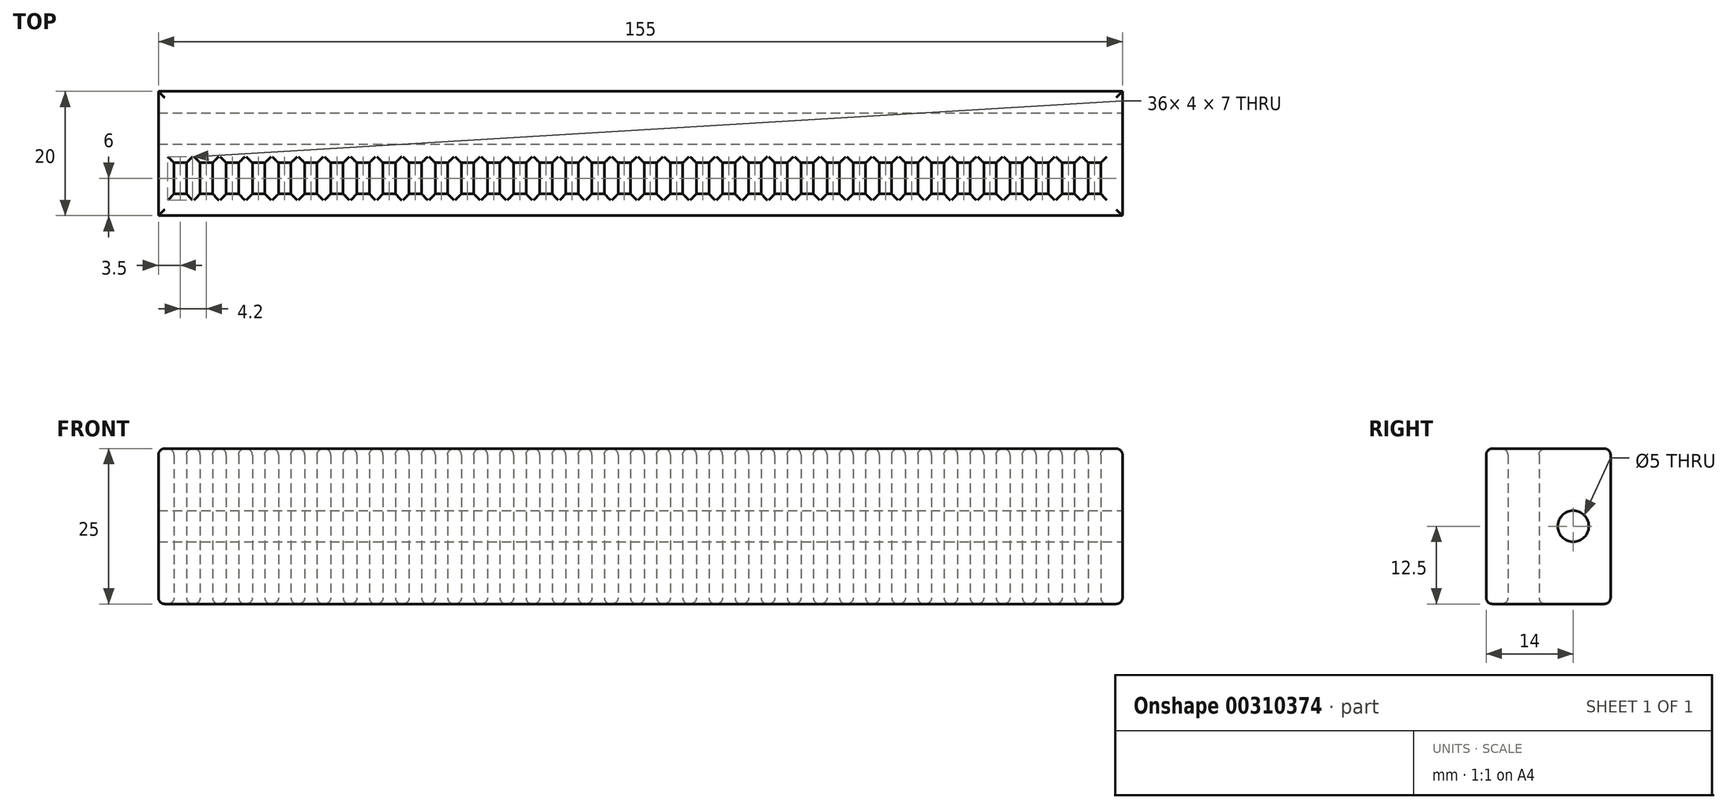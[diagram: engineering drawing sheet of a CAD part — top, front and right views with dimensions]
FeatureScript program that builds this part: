
annotation { "Feature Type Name" : "Feature", "Feature Type Description" : "" }
export const myFeature = defineFeature(function(context is Context, id is Id, definition is map)
    precondition{}
    {
        {
            var Q0;
            Q0=qCreatedBy(makeId("Top.planeOp"),FACE);
            var sketch = newSketch(context, id + "F0", { "sketchPlane" : qUnion([Q0])});
            skLineSegment(sketch, "E0.bottom", {"start": v(77.5, -10) * mm, "end": v(-77.5, -10) * mm});
            skLineSegment(sketch, "E0.top", {"start": v(77.5, 10) * mm, "end": v(-77.5, 10) * mm});
            skLineSegment(sketch, "E0.left", {"start": v(77.5, -10) * mm, "end": v(77.5, 10) * mm});
            skLineSegment(sketch, "E0.right", {"start": v(-77.5, -10) * mm, "end": v(-77.5, 10) * mm});
            skPoint(sketch, "E0.middle", {"position": v(0, 0) * mm});
            skLineSegment(sketch, "E1.bottom", {"start": v(-75, -1.5) * mm, "end": v(-73, -1.5) * mm});
            skLineSegment(sketch, "E1.top", {"start": v(-75, -6.5) * mm, "end": v(-73, -6.5) * mm});
            skLineSegment(sketch, "E1.left", {"start": v(-75, -1.5) * mm, "end": v(-75, -6.5) * mm});
            skLineSegment(sketch, "E1.right", {"start": v(-73, -1.5) * mm, "end": v(-73, -6.5) * mm});
            skLineSegment(sketch, "E2.1.0.0", {"start": v(-70.8, -1.5) * mm, "end": v(-68.8, -1.5) * mm});
            skLineSegment(sketch, "E2.1.0.1", {"start": v(-68.8, -1.5) * mm, "end": v(-68.8, -6.5) * mm});
            skLineSegment(sketch, "E2.1.0.2", {"start": v(-70.8, -6.5) * mm, "end": v(-68.8, -6.5) * mm});
            skLineSegment(sketch, "E2.1.0.3", {"start": v(-70.8, -1.5) * mm, "end": v(-70.8, -6.5) * mm});
            skLineSegment(sketch, "E2.2.0.0", {"start": v(-66.6, -1.5) * mm, "end": v(-64.6, -1.5) * mm});
            skLineSegment(sketch, "E2.2.0.1", {"start": v(-64.6, -1.5) * mm, "end": v(-64.6, -6.5) * mm});
            skLineSegment(sketch, "E2.2.0.2", {"start": v(-66.6, -6.5) * mm, "end": v(-64.6, -6.5) * mm});
            skLineSegment(sketch, "E2.2.0.3", {"start": v(-66.6, -1.5) * mm, "end": v(-66.6, -6.5) * mm});
            skLineSegment(sketch, "E2.3.0.0", {"start": v(-62.4, -1.5) * mm, "end": v(-60.4, -1.5) * mm});
            skLineSegment(sketch, "E2.3.0.1", {"start": v(-60.4, -1.5) * mm, "end": v(-60.4, -6.5) * mm});
            skLineSegment(sketch, "E2.3.0.2", {"start": v(-62.4, -6.5) * mm, "end": v(-60.4, -6.5) * mm});
            skLineSegment(sketch, "E2.3.0.3", {"start": v(-62.4, -1.5) * mm, "end": v(-62.4, -6.5) * mm});
            skLineSegment(sketch, "E2.4.0.0", {"start": v(-58.2, -1.5) * mm, "end": v(-56.2, -1.5) * mm});
            skLineSegment(sketch, "E2.4.0.1", {"start": v(-56.2, -1.5) * mm, "end": v(-56.2, -6.5) * mm});
            skLineSegment(sketch, "E2.4.0.2", {"start": v(-58.2, -6.5) * mm, "end": v(-56.2, -6.5) * mm});
            skLineSegment(sketch, "E2.4.0.3", {"start": v(-58.2, -1.5) * mm, "end": v(-58.2, -6.5) * mm});
            skLineSegment(sketch, "E2.5.0.0", {"start": v(-54, -1.5) * mm, "end": v(-52, -1.5) * mm});
            skLineSegment(sketch, "E2.5.0.1", {"start": v(-52, -1.5) * mm, "end": v(-52, -6.5) * mm});
            skLineSegment(sketch, "E2.5.0.2", {"start": v(-54, -6.5) * mm, "end": v(-52, -6.5) * mm});
            skLineSegment(sketch, "E2.5.0.3", {"start": v(-54, -1.5) * mm, "end": v(-54, -6.5) * mm});
            skLineSegment(sketch, "E2.6.0.0", {"start": v(-49.8, -1.5) * mm, "end": v(-47.8, -1.5) * mm});
            skLineSegment(sketch, "E2.6.0.1", {"start": v(-47.8, -1.5) * mm, "end": v(-47.8, -6.5) * mm});
            skLineSegment(sketch, "E2.6.0.2", {"start": v(-49.8, -6.5) * mm, "end": v(-47.8, -6.5) * mm});
            skLineSegment(sketch, "E2.6.0.3", {"start": v(-49.8, -1.5) * mm, "end": v(-49.8, -6.5) * mm});
            skLineSegment(sketch, "E2.7.0.0", {"start": v(-45.6, -1.5) * mm, "end": v(-43.6, -1.5) * mm});
            skLineSegment(sketch, "E2.7.0.1", {"start": v(-43.6, -1.5) * mm, "end": v(-43.6, -6.5) * mm});
            skLineSegment(sketch, "E2.7.0.2", {"start": v(-45.6, -6.5) * mm, "end": v(-43.6, -6.5) * mm});
            skLineSegment(sketch, "E2.7.0.3", {"start": v(-45.6, -1.5) * mm, "end": v(-45.6, -6.5) * mm});
            skLineSegment(sketch, "E2.8.0.0", {"start": v(-41.4, -1.5) * mm, "end": v(-39.4, -1.5) * mm});
            skLineSegment(sketch, "E2.8.0.1", {"start": v(-39.4, -1.5) * mm, "end": v(-39.4, -6.5) * mm});
            skLineSegment(sketch, "E2.8.0.2", {"start": v(-41.4, -6.5) * mm, "end": v(-39.4, -6.5) * mm});
            skLineSegment(sketch, "E2.8.0.3", {"start": v(-41.4, -1.5) * mm, "end": v(-41.4, -6.5) * mm});
            skLineSegment(sketch, "E2.9.0.0", {"start": v(-37.2, -1.5) * mm, "end": v(-35.2, -1.5) * mm});
            skLineSegment(sketch, "E2.9.0.1", {"start": v(-35.2, -1.5) * mm, "end": v(-35.2, -6.5) * mm});
            skLineSegment(sketch, "E2.9.0.2", {"start": v(-37.2, -6.5) * mm, "end": v(-35.2, -6.5) * mm});
            skLineSegment(sketch, "E2.9.0.3", {"start": v(-37.2, -1.5) * mm, "end": v(-37.2, -6.5) * mm});
            skLineSegment(sketch, "E2.10.0.0", {"start": v(-33, -1.5) * mm, "end": v(-31, -1.5) * mm});
            skLineSegment(sketch, "E2.10.0.1", {"start": v(-31, -1.5) * mm, "end": v(-31, -6.5) * mm});
            skLineSegment(sketch, "E2.10.0.2", {"start": v(-33, -6.5) * mm, "end": v(-31, -6.5) * mm});
            skLineSegment(sketch, "E2.10.0.3", {"start": v(-33, -1.5) * mm, "end": v(-33, -6.5) * mm});
            skLineSegment(sketch, "E2.11.0.0", {"start": v(-28.8, -1.5) * mm, "end": v(-26.8, -1.5) * mm});
            skLineSegment(sketch, "E2.11.0.1", {"start": v(-26.8, -1.5) * mm, "end": v(-26.8, -6.5) * mm});
            skLineSegment(sketch, "E2.11.0.2", {"start": v(-28.8, -6.5) * mm, "end": v(-26.8, -6.5) * mm});
            skLineSegment(sketch, "E2.11.0.3", {"start": v(-28.8, -1.5) * mm, "end": v(-28.8, -6.5) * mm});
            skLineSegment(sketch, "E2.12.0.0", {"start": v(-24.6, -1.5) * mm, "end": v(-22.6, -1.5) * mm});
            skLineSegment(sketch, "E2.12.0.1", {"start": v(-22.6, -1.5) * mm, "end": v(-22.6, -6.5) * mm});
            skLineSegment(sketch, "E2.12.0.2", {"start": v(-24.6, -6.5) * mm, "end": v(-22.6, -6.5) * mm});
            skLineSegment(sketch, "E2.12.0.3", {"start": v(-24.6, -1.5) * mm, "end": v(-24.6, -6.5) * mm});
            skLineSegment(sketch, "E2.13.0.0", {"start": v(-20.4, -1.5) * mm, "end": v(-18.4, -1.5) * mm});
            skLineSegment(sketch, "E2.13.0.1", {"start": v(-18.4, -1.5) * mm, "end": v(-18.4, -6.5) * mm});
            skLineSegment(sketch, "E2.13.0.2", {"start": v(-20.4, -6.5) * mm, "end": v(-18.4, -6.5) * mm});
            skLineSegment(sketch, "E2.13.0.3", {"start": v(-20.4, -1.5) * mm, "end": v(-20.4, -6.5) * mm});
            skLineSegment(sketch, "E2.14.0.0", {"start": v(-16.2, -1.5) * mm, "end": v(-14.2, -1.5) * mm});
            skLineSegment(sketch, "E2.14.0.1", {"start": v(-14.2, -1.5) * mm, "end": v(-14.2, -6.5) * mm});
            skLineSegment(sketch, "E2.14.0.2", {"start": v(-16.2, -6.5) * mm, "end": v(-14.2, -6.5) * mm});
            skLineSegment(sketch, "E2.14.0.3", {"start": v(-16.2, -1.5) * mm, "end": v(-16.2, -6.5) * mm});
            skLineSegment(sketch, "E2.15.0.0", {"start": v(-12, -1.5) * mm, "end": v(-10, -1.5) * mm});
            skLineSegment(sketch, "E2.15.0.1", {"start": v(-10, -1.5) * mm, "end": v(-10, -6.5) * mm});
            skLineSegment(sketch, "E2.15.0.2", {"start": v(-12, -6.5) * mm, "end": v(-10, -6.5) * mm});
            skLineSegment(sketch, "E2.15.0.3", {"start": v(-12, -1.5) * mm, "end": v(-12, -6.5) * mm});
            skLineSegment(sketch, "E2.16.0.0", {"start": v(-7.8, -1.5) * mm, "end": v(-5.8, -1.5) * mm});
            skLineSegment(sketch, "E2.16.0.1", {"start": v(-5.8, -1.5) * mm, "end": v(-5.8, -6.5) * mm});
            skLineSegment(sketch, "E2.16.0.2", {"start": v(-7.8, -6.5) * mm, "end": v(-5.8, -6.5) * mm});
            skLineSegment(sketch, "E2.16.0.3", {"start": v(-7.8, -1.5) * mm, "end": v(-7.8, -6.5) * mm});
            skLineSegment(sketch, "E2.17.0.0", {"start": v(-3.6, -1.5) * mm, "end": v(-1.6, -1.5) * mm});
            skLineSegment(sketch, "E2.17.0.1", {"start": v(-1.6, -1.5) * mm, "end": v(-1.6, -6.5) * mm});
            skLineSegment(sketch, "E2.17.0.2", {"start": v(-3.6, -6.5) * mm, "end": v(-1.6, -6.5) * mm});
            skLineSegment(sketch, "E2.17.0.3", {"start": v(-3.6, -1.5) * mm, "end": v(-3.6, -6.5) * mm});
            skLineSegment(sketch, "E2.18.0.0", {"start": v(0.6, -1.5) * mm, "end": v(2.6, -1.5) * mm});
            skLineSegment(sketch, "E2.18.0.1", {"start": v(2.6, -1.5) * mm, "end": v(2.6, -6.5) * mm});
            skLineSegment(sketch, "E2.18.0.2", {"start": v(0.6, -6.5) * mm, "end": v(2.6, -6.5) * mm});
            skLineSegment(sketch, "E2.18.0.3", {"start": v(0.6, -1.5) * mm, "end": v(0.6, -6.5) * mm});
            skLineSegment(sketch, "E2.19.0.0", {"start": v(4.8, -1.5) * mm, "end": v(6.8, -1.5) * mm});
            skLineSegment(sketch, "E2.19.0.1", {"start": v(6.8, -1.5) * mm, "end": v(6.8, -6.5) * mm});
            skLineSegment(sketch, "E2.19.0.2", {"start": v(4.8, -6.5) * mm, "end": v(6.8, -6.5) * mm});
            skLineSegment(sketch, "E2.19.0.3", {"start": v(4.8, -1.5) * mm, "end": v(4.8, -6.5) * mm});
            skLineSegment(sketch, "E2.20.0.0", {"start": v(9, -1.5) * mm, "end": v(11, -1.5) * mm});
            skLineSegment(sketch, "E2.20.0.1", {"start": v(11, -1.5) * mm, "end": v(11, -6.5) * mm});
            skLineSegment(sketch, "E2.20.0.2", {"start": v(9, -6.5) * mm, "end": v(11, -6.5) * mm});
            skLineSegment(sketch, "E2.20.0.3", {"start": v(9, -1.5) * mm, "end": v(9, -6.5) * mm});
            skLineSegment(sketch, "E2.21.0.0", {"start": v(13.2, -1.5) * mm, "end": v(15.2, -1.5) * mm});
            skLineSegment(sketch, "E2.21.0.1", {"start": v(15.2, -1.5) * mm, "end": v(15.2, -6.5) * mm});
            skLineSegment(sketch, "E2.21.0.2", {"start": v(13.2, -6.5) * mm, "end": v(15.2, -6.5) * mm});
            skLineSegment(sketch, "E2.21.0.3", {"start": v(13.2, -1.5) * mm, "end": v(13.2, -6.5) * mm});
            skLineSegment(sketch, "E2.22.0.0", {"start": v(17.4, -1.5) * mm, "end": v(19.4, -1.5) * mm});
            skLineSegment(sketch, "E2.22.0.1", {"start": v(19.4, -1.5) * mm, "end": v(19.4, -6.5) * mm});
            skLineSegment(sketch, "E2.22.0.2", {"start": v(17.4, -6.5) * mm, "end": v(19.4, -6.5) * mm});
            skLineSegment(sketch, "E2.22.0.3", {"start": v(17.4, -1.5) * mm, "end": v(17.4, -6.5) * mm});
            skLineSegment(sketch, "E2.23.0.0", {"start": v(21.6, -1.5) * mm, "end": v(23.6, -1.5) * mm});
            skLineSegment(sketch, "E2.23.0.1", {"start": v(23.6, -1.5) * mm, "end": v(23.6, -6.5) * mm});
            skLineSegment(sketch, "E2.23.0.2", {"start": v(21.6, -6.5) * mm, "end": v(23.6, -6.5) * mm});
            skLineSegment(sketch, "E2.23.0.3", {"start": v(21.6, -1.5) * mm, "end": v(21.6, -6.5) * mm});
            skLineSegment(sketch, "E2.24.0.0", {"start": v(25.8, -1.5) * mm, "end": v(27.8, -1.5) * mm});
            skLineSegment(sketch, "E2.24.0.1", {"start": v(27.8, -1.5) * mm, "end": v(27.8, -6.5) * mm});
            skLineSegment(sketch, "E2.24.0.2", {"start": v(25.8, -6.5) * mm, "end": v(27.8, -6.5) * mm});
            skLineSegment(sketch, "E2.24.0.3", {"start": v(25.8, -1.5) * mm, "end": v(25.8, -6.5) * mm});
            skLineSegment(sketch, "E2.25.0.0", {"start": v(30, -1.5) * mm, "end": v(32, -1.5) * mm});
            skLineSegment(sketch, "E2.25.0.1", {"start": v(32, -1.5) * mm, "end": v(32, -6.5) * mm});
            skLineSegment(sketch, "E2.25.0.2", {"start": v(30, -6.5) * mm, "end": v(32, -6.5) * mm});
            skLineSegment(sketch, "E2.25.0.3", {"start": v(30, -1.5) * mm, "end": v(30, -6.5) * mm});
            skLineSegment(sketch, "E2.26.0.0", {"start": v(34.2, -1.5) * mm, "end": v(36.2, -1.5) * mm});
            skLineSegment(sketch, "E2.26.0.1", {"start": v(36.2, -1.5) * mm, "end": v(36.2, -6.5) * mm});
            skLineSegment(sketch, "E2.26.0.2", {"start": v(34.2, -6.5) * mm, "end": v(36.2, -6.5) * mm});
            skLineSegment(sketch, "E2.26.0.3", {"start": v(34.2, -1.5) * mm, "end": v(34.2, -6.5) * mm});
            skLineSegment(sketch, "E2.27.0.0", {"start": v(38.4, -1.5) * mm, "end": v(40.4, -1.5) * mm});
            skLineSegment(sketch, "E2.27.0.1", {"start": v(40.4, -1.5) * mm, "end": v(40.4, -6.5) * mm});
            skLineSegment(sketch, "E2.27.0.2", {"start": v(38.4, -6.5) * mm, "end": v(40.4, -6.5) * mm});
            skLineSegment(sketch, "E2.27.0.3", {"start": v(38.4, -1.5) * mm, "end": v(38.4, -6.5) * mm});
            skLineSegment(sketch, "E2.28.0.0", {"start": v(42.6, -1.5) * mm, "end": v(44.6, -1.5) * mm});
            skLineSegment(sketch, "E2.28.0.1", {"start": v(44.6, -1.5) * mm, "end": v(44.6, -6.5) * mm});
            skLineSegment(sketch, "E2.28.0.2", {"start": v(42.6, -6.5) * mm, "end": v(44.6, -6.5) * mm});
            skLineSegment(sketch, "E2.28.0.3", {"start": v(42.6, -1.5) * mm, "end": v(42.6, -6.5) * mm});
            skLineSegment(sketch, "E2.29.0.0", {"start": v(46.8, -1.5) * mm, "end": v(48.8, -1.5) * mm});
            skLineSegment(sketch, "E2.29.0.1", {"start": v(48.8, -1.5) * mm, "end": v(48.8, -6.5) * mm});
            skLineSegment(sketch, "E2.29.0.2", {"start": v(46.8, -6.5) * mm, "end": v(48.8, -6.5) * mm});
            skLineSegment(sketch, "E2.29.0.3", {"start": v(46.8, -1.5) * mm, "end": v(46.8, -6.5) * mm});
            skLineSegment(sketch, "E2.30.0.0", {"start": v(51, -1.5) * mm, "end": v(53, -1.5) * mm});
            skLineSegment(sketch, "E2.30.0.1", {"start": v(53, -1.5) * mm, "end": v(53, -6.5) * mm});
            skLineSegment(sketch, "E2.30.0.2", {"start": v(51, -6.5) * mm, "end": v(53, -6.5) * mm});
            skLineSegment(sketch, "E2.30.0.3", {"start": v(51, -1.5) * mm, "end": v(51, -6.5) * mm});
            skLineSegment(sketch, "E2.31.0.0", {"start": v(55.2, -1.5) * mm, "end": v(57.2, -1.5) * mm});
            skLineSegment(sketch, "E2.31.0.1", {"start": v(57.2, -1.5) * mm, "end": v(57.2, -6.5) * mm});
            skLineSegment(sketch, "E2.31.0.2", {"start": v(55.2, -6.5) * mm, "end": v(57.2, -6.5) * mm});
            skLineSegment(sketch, "E2.31.0.3", {"start": v(55.2, -1.5) * mm, "end": v(55.2, -6.5) * mm});
            skLineSegment(sketch, "E2.32.0.0", {"start": v(59.4, -1.5) * mm, "end": v(61.4, -1.5) * mm});
            skLineSegment(sketch, "E2.32.0.1", {"start": v(61.4, -1.5) * mm, "end": v(61.4, -6.5) * mm});
            skLineSegment(sketch, "E2.32.0.2", {"start": v(59.4, -6.5) * mm, "end": v(61.4, -6.5) * mm});
            skLineSegment(sketch, "E2.32.0.3", {"start": v(59.4, -1.5) * mm, "end": v(59.4, -6.5) * mm});
            skLineSegment(sketch, "E2.33.0.0", {"start": v(63.6, -1.5) * mm, "end": v(65.6, -1.5) * mm});
            skLineSegment(sketch, "E2.33.0.1", {"start": v(65.6, -1.5) * mm, "end": v(65.6, -6.5) * mm});
            skLineSegment(sketch, "E2.33.0.2", {"start": v(63.6, -6.5) * mm, "end": v(65.6, -6.5) * mm});
            skLineSegment(sketch, "E2.33.0.3", {"start": v(63.6, -1.5) * mm, "end": v(63.6, -6.5) * mm});
            skLineSegment(sketch, "E2.34.0.0", {"start": v(67.8, -1.5) * mm, "end": v(69.8, -1.5) * mm});
            skLineSegment(sketch, "E2.34.0.1", {"start": v(69.8, -1.5) * mm, "end": v(69.8, -6.5) * mm});
            skLineSegment(sketch, "E2.34.0.2", {"start": v(67.8, -6.5) * mm, "end": v(69.8, -6.5) * mm});
            skLineSegment(sketch, "E2.34.0.3", {"start": v(67.8, -1.5) * mm, "end": v(67.8, -6.5) * mm});
            skLineSegment(sketch, "E2.35.0.0", {"start": v(72, -1.5) * mm, "end": v(74, -1.5) * mm});
            skLineSegment(sketch, "E2.35.0.1", {"start": v(74, -1.5) * mm, "end": v(74, -6.5) * mm});
            skLineSegment(sketch, "E2.35.0.2", {"start": v(72, -6.5) * mm, "end": v(74, -6.5) * mm});
            skLineSegment(sketch, "E2.35.0.3", {"start": v(72, -1.5) * mm, "end": v(72, -6.5) * mm});
            skLineSegment(sketch, "E2.direction1", {"start": v(-75, -1.5) * mm, "end": v(-70.8, -1.5) * mm, "construction": true});
            skSolve(sketch);
        }
        {
            var Q0;
            Q0 = qSketchRegion(id + "F0", true);
            extrude(context, id + "F1", {"entities" : qUnion([Q0]), "depth" : 25 * mm, "offsetDistance" : 25 * mm});
        }
        {
            var Q0;
            Q0=makeQuery(id+"F1.opExtrude","CAP_FACE",FACE,{"disambiguationData":[OSD([sQuery(id+"F0.wireOp",EDGE,"E0.bottom"),sQuery(id+"F0.wireOp",EDGE,"E0.top"),sQuery(id+"F0.wireOp",EDGE,"E0.left"),sQuery(id+"F0.wireOp",EDGE,"E0.right"),sQuery(id+"F0.wireOp",EDGE,"E1.bottom"),sQuery(id+"F0.wireOp",EDGE,"E1.top"),sQuery(id+"F0.wireOp",EDGE,"E1.left"),sQuery(id+"F0.wireOp",EDGE,"E1.right"),sQuery(id+"F0.wireOp",EDGE,"E2.1.0.0"),sQuery(id+"F0.wireOp",EDGE,"E2.1.0.1"),sQuery(id+"F0.wireOp",EDGE,"E2.1.0.2"),sQuery(id+"F0.wireOp",EDGE,"E2.1.0.3"),sQuery(id+"F0.wireOp",EDGE,"E2.2.0.0"),sQuery(id+"F0.wireOp",EDGE,"E2.2.0.1"),sQuery(id+"F0.wireOp",EDGE,"E2.2.0.2"),sQuery(id+"F0.wireOp",EDGE,"E2.2.0.3"),sQuery(id+"F0.wireOp",EDGE,"E2.3.0.0"),sQuery(id+"F0.wireOp",EDGE,"E2.3.0.1"),sQuery(id+"F0.wireOp",EDGE,"E2.3.0.2"),sQuery(id+"F0.wireOp",EDGE,"E2.3.0.3"),sQuery(id+"F0.wireOp",EDGE,"E2.4.0.0"),sQuery(id+"F0.wireOp",EDGE,"E2.4.0.1"),sQuery(id+"F0.wireOp",EDGE,"E2.4.0.2"),sQuery(id+"F0.wireOp",EDGE,"E2.4.0.3"),sQuery(id+"F0.wireOp",EDGE,"E2.5.0.0"),sQuery(id+"F0.wireOp",EDGE,"E2.5.0.1"),sQuery(id+"F0.wireOp",EDGE,"E2.5.0.2"),sQuery(id+"F0.wireOp",EDGE,"E2.5.0.3"),sQuery(id+"F0.wireOp",EDGE,"E2.6.0.0"),sQuery(id+"F0.wireOp",EDGE,"E2.6.0.1"),sQuery(id+"F0.wireOp",EDGE,"E2.6.0.2"),sQuery(id+"F0.wireOp",EDGE,"E2.6.0.3"),sQuery(id+"F0.wireOp",EDGE,"E2.7.0.0"),sQuery(id+"F0.wireOp",EDGE,"E2.7.0.1"),sQuery(id+"F0.wireOp",EDGE,"E2.7.0.2"),sQuery(id+"F0.wireOp",EDGE,"E2.7.0.3"),sQuery(id+"F0.wireOp",EDGE,"E2.8.0.0"),sQuery(id+"F0.wireOp",EDGE,"E2.8.0.1"),sQuery(id+"F0.wireOp",EDGE,"E2.8.0.2"),sQuery(id+"F0.wireOp",EDGE,"E2.8.0.3"),sQuery(id+"F0.wireOp",EDGE,"E2.9.0.0"),sQuery(id+"F0.wireOp",EDGE,"E2.9.0.1"),sQuery(id+"F0.wireOp",EDGE,"E2.9.0.2"),sQuery(id+"F0.wireOp",EDGE,"E2.9.0.3"),sQuery(id+"F0.wireOp",EDGE,"E2.10.0.0"),sQuery(id+"F0.wireOp",EDGE,"E2.10.0.1"),sQuery(id+"F0.wireOp",EDGE,"E2.10.0.2"),sQuery(id+"F0.wireOp",EDGE,"E2.10.0.3"),sQuery(id+"F0.wireOp",EDGE,"E2.11.0.0"),sQuery(id+"F0.wireOp",EDGE,"E2.11.0.1"),sQuery(id+"F0.wireOp",EDGE,"E2.11.0.2"),sQuery(id+"F0.wireOp",EDGE,"E2.11.0.3"),sQuery(id+"F0.wireOp",EDGE,"E2.12.0.0"),sQuery(id+"F0.wireOp",EDGE,"E2.12.0.1"),sQuery(id+"F0.wireOp",EDGE,"E2.12.0.2"),sQuery(id+"F0.wireOp",EDGE,"E2.12.0.3"),sQuery(id+"F0.wireOp",EDGE,"E2.13.0.0"),sQuery(id+"F0.wireOp",EDGE,"E2.13.0.1"),sQuery(id+"F0.wireOp",EDGE,"E2.13.0.2"),sQuery(id+"F0.wireOp",EDGE,"E2.13.0.3"),sQuery(id+"F0.wireOp",EDGE,"E2.14.0.0"),sQuery(id+"F0.wireOp",EDGE,"E2.14.0.1"),sQuery(id+"F0.wireOp",EDGE,"E2.14.0.2"),sQuery(id+"F0.wireOp",EDGE,"E2.14.0.3"),sQuery(id+"F0.wireOp",EDGE,"E2.15.0.0"),sQuery(id+"F0.wireOp",EDGE,"E2.15.0.1"),sQuery(id+"F0.wireOp",EDGE,"E2.15.0.2"),sQuery(id+"F0.wireOp",EDGE,"E2.15.0.3"),sQuery(id+"F0.wireOp",EDGE,"E2.16.0.0"),sQuery(id+"F0.wireOp",EDGE,"E2.16.0.1"),sQuery(id+"F0.wireOp",EDGE,"E2.16.0.2"),sQuery(id+"F0.wireOp",EDGE,"E2.16.0.3"),sQuery(id+"F0.wireOp",EDGE,"E2.17.0.0"),sQuery(id+"F0.wireOp",EDGE,"E2.17.0.1"),sQuery(id+"F0.wireOp",EDGE,"E2.17.0.2"),sQuery(id+"F0.wireOp",EDGE,"E2.17.0.3"),sQuery(id+"F0.wireOp",EDGE,"E2.18.0.0"),sQuery(id+"F0.wireOp",EDGE,"E2.18.0.1"),sQuery(id+"F0.wireOp",EDGE,"E2.18.0.2"),sQuery(id+"F0.wireOp",EDGE,"E2.18.0.3"),sQuery(id+"F0.wireOp",EDGE,"E2.19.0.0"),sQuery(id+"F0.wireOp",EDGE,"E2.19.0.1"),sQuery(id+"F0.wireOp",EDGE,"E2.19.0.2"),sQuery(id+"F0.wireOp",EDGE,"E2.19.0.3"),sQuery(id+"F0.wireOp",EDGE,"E2.20.0.0"),sQuery(id+"F0.wireOp",EDGE,"E2.20.0.1"),sQuery(id+"F0.wireOp",EDGE,"E2.20.0.2"),sQuery(id+"F0.wireOp",EDGE,"E2.20.0.3"),sQuery(id+"F0.wireOp",EDGE,"E2.21.0.0"),sQuery(id+"F0.wireOp",EDGE,"E2.21.0.1"),sQuery(id+"F0.wireOp",EDGE,"E2.21.0.2"),sQuery(id+"F0.wireOp",EDGE,"E2.21.0.3"),sQuery(id+"F0.wireOp",EDGE,"E2.22.0.0"),sQuery(id+"F0.wireOp",EDGE,"E2.22.0.1"),sQuery(id+"F0.wireOp",EDGE,"E2.22.0.2"),sQuery(id+"F0.wireOp",EDGE,"E2.22.0.3"),sQuery(id+"F0.wireOp",EDGE,"E2.23.0.0"),sQuery(id+"F0.wireOp",EDGE,"E2.23.0.1"),sQuery(id+"F0.wireOp",EDGE,"E2.23.0.2"),sQuery(id+"F0.wireOp",EDGE,"E2.23.0.3"),sQuery(id+"F0.wireOp",EDGE,"E2.24.0.0"),sQuery(id+"F0.wireOp",EDGE,"E2.24.0.1"),sQuery(id+"F0.wireOp",EDGE,"E2.24.0.2"),sQuery(id+"F0.wireOp",EDGE,"E2.24.0.3"),sQuery(id+"F0.wireOp",EDGE,"E2.25.0.0"),sQuery(id+"F0.wireOp",EDGE,"E2.25.0.1"),sQuery(id+"F0.wireOp",EDGE,"E2.25.0.2"),sQuery(id+"F0.wireOp",EDGE,"E2.25.0.3"),sQuery(id+"F0.wireOp",EDGE,"E2.26.0.0"),sQuery(id+"F0.wireOp",EDGE,"E2.26.0.1"),sQuery(id+"F0.wireOp",EDGE,"E2.26.0.2"),sQuery(id+"F0.wireOp",EDGE,"E2.26.0.3"),sQuery(id+"F0.wireOp",EDGE,"E2.27.0.0"),sQuery(id+"F0.wireOp",EDGE,"E2.27.0.1"),sQuery(id+"F0.wireOp",EDGE,"E2.27.0.2"),sQuery(id+"F0.wireOp",EDGE,"E2.27.0.3"),sQuery(id+"F0.wireOp",EDGE,"E2.28.0.0"),sQuery(id+"F0.wireOp",EDGE,"E2.28.0.1"),sQuery(id+"F0.wireOp",EDGE,"E2.28.0.2"),sQuery(id+"F0.wireOp",EDGE,"E2.28.0.3"),sQuery(id+"F0.wireOp",EDGE,"E2.29.0.0"),sQuery(id+"F0.wireOp",EDGE,"E2.29.0.1"),sQuery(id+"F0.wireOp",EDGE,"E2.29.0.2"),sQuery(id+"F0.wireOp",EDGE,"E2.29.0.3"),sQuery(id+"F0.wireOp",EDGE,"E2.30.0.0"),sQuery(id+"F0.wireOp",EDGE,"E2.30.0.1"),sQuery(id+"F0.wireOp",EDGE,"E2.30.0.2"),sQuery(id+"F0.wireOp",EDGE,"E2.30.0.3"),sQuery(id+"F0.wireOp",EDGE,"E2.31.0.0"),sQuery(id+"F0.wireOp",EDGE,"E2.31.0.1"),sQuery(id+"F0.wireOp",EDGE,"E2.31.0.2"),sQuery(id+"F0.wireOp",EDGE,"E2.31.0.3"),sQuery(id+"F0.wireOp",EDGE,"E2.32.0.0"),sQuery(id+"F0.wireOp",EDGE,"E2.32.0.1"),sQuery(id+"F0.wireOp",EDGE,"E2.32.0.2"),sQuery(id+"F0.wireOp",EDGE,"E2.32.0.3"),sQuery(id+"F0.wireOp",EDGE,"E2.33.0.0"),sQuery(id+"F0.wireOp",EDGE,"E2.33.0.1"),sQuery(id+"F0.wireOp",EDGE,"E2.33.0.2"),sQuery(id+"F0.wireOp",EDGE,"E2.33.0.3"),sQuery(id+"F0.wireOp",EDGE,"E2.34.0.0"),sQuery(id+"F0.wireOp",EDGE,"E2.34.0.1"),sQuery(id+"F0.wireOp",EDGE,"E2.34.0.2"),sQuery(id+"F0.wireOp",EDGE,"E2.34.0.3"),sQuery(id+"F0.wireOp",EDGE,"E2.35.0.0"),sQuery(id+"F0.wireOp",EDGE,"E2.35.0.1"),sQuery(id+"F0.wireOp",EDGE,"E2.35.0.2"),sQuery(id+"F0.wireOp",EDGE,"E2.35.0.3")])],"isStart":false});
            fillet(context, id + "F2", {"entities" : qUnion([Q0]), "radius" : 1 * mm, "tangentPropagation" : true, "allowEdgeOverflow" : false});
        }
        {
            var Q0;
            Q0=makeQuery(id+"F1.opExtrude","CAP_FACE",FACE,{"disambiguationData":[OSD([sQuery(id+"F0.wireOp",EDGE,"E0.bottom"),sQuery(id+"F0.wireOp",EDGE,"E0.top"),sQuery(id+"F0.wireOp",EDGE,"E0.left"),sQuery(id+"F0.wireOp",EDGE,"E0.right"),sQuery(id+"F0.wireOp",EDGE,"E1.bottom"),sQuery(id+"F0.wireOp",EDGE,"E1.top"),sQuery(id+"F0.wireOp",EDGE,"E1.left"),sQuery(id+"F0.wireOp",EDGE,"E1.right"),sQuery(id+"F0.wireOp",EDGE,"E2.1.0.0"),sQuery(id+"F0.wireOp",EDGE,"E2.1.0.1"),sQuery(id+"F0.wireOp",EDGE,"E2.1.0.2"),sQuery(id+"F0.wireOp",EDGE,"E2.1.0.3"),sQuery(id+"F0.wireOp",EDGE,"E2.2.0.0"),sQuery(id+"F0.wireOp",EDGE,"E2.2.0.1"),sQuery(id+"F0.wireOp",EDGE,"E2.2.0.2"),sQuery(id+"F0.wireOp",EDGE,"E2.2.0.3"),sQuery(id+"F0.wireOp",EDGE,"E2.3.0.0"),sQuery(id+"F0.wireOp",EDGE,"E2.3.0.1"),sQuery(id+"F0.wireOp",EDGE,"E2.3.0.2"),sQuery(id+"F0.wireOp",EDGE,"E2.3.0.3"),sQuery(id+"F0.wireOp",EDGE,"E2.4.0.0"),sQuery(id+"F0.wireOp",EDGE,"E2.4.0.1"),sQuery(id+"F0.wireOp",EDGE,"E2.4.0.2"),sQuery(id+"F0.wireOp",EDGE,"E2.4.0.3"),sQuery(id+"F0.wireOp",EDGE,"E2.5.0.0"),sQuery(id+"F0.wireOp",EDGE,"E2.5.0.1"),sQuery(id+"F0.wireOp",EDGE,"E2.5.0.2"),sQuery(id+"F0.wireOp",EDGE,"E2.5.0.3"),sQuery(id+"F0.wireOp",EDGE,"E2.6.0.0"),sQuery(id+"F0.wireOp",EDGE,"E2.6.0.1"),sQuery(id+"F0.wireOp",EDGE,"E2.6.0.2"),sQuery(id+"F0.wireOp",EDGE,"E2.6.0.3"),sQuery(id+"F0.wireOp",EDGE,"E2.7.0.0"),sQuery(id+"F0.wireOp",EDGE,"E2.7.0.1"),sQuery(id+"F0.wireOp",EDGE,"E2.7.0.2"),sQuery(id+"F0.wireOp",EDGE,"E2.7.0.3"),sQuery(id+"F0.wireOp",EDGE,"E2.8.0.0"),sQuery(id+"F0.wireOp",EDGE,"E2.8.0.1"),sQuery(id+"F0.wireOp",EDGE,"E2.8.0.2"),sQuery(id+"F0.wireOp",EDGE,"E2.8.0.3"),sQuery(id+"F0.wireOp",EDGE,"E2.9.0.0"),sQuery(id+"F0.wireOp",EDGE,"E2.9.0.1"),sQuery(id+"F0.wireOp",EDGE,"E2.9.0.2"),sQuery(id+"F0.wireOp",EDGE,"E2.9.0.3"),sQuery(id+"F0.wireOp",EDGE,"E2.10.0.0"),sQuery(id+"F0.wireOp",EDGE,"E2.10.0.1"),sQuery(id+"F0.wireOp",EDGE,"E2.10.0.2"),sQuery(id+"F0.wireOp",EDGE,"E2.10.0.3"),sQuery(id+"F0.wireOp",EDGE,"E2.11.0.0"),sQuery(id+"F0.wireOp",EDGE,"E2.11.0.1"),sQuery(id+"F0.wireOp",EDGE,"E2.11.0.2"),sQuery(id+"F0.wireOp",EDGE,"E2.11.0.3"),sQuery(id+"F0.wireOp",EDGE,"E2.12.0.0"),sQuery(id+"F0.wireOp",EDGE,"E2.12.0.1"),sQuery(id+"F0.wireOp",EDGE,"E2.12.0.2"),sQuery(id+"F0.wireOp",EDGE,"E2.12.0.3"),sQuery(id+"F0.wireOp",EDGE,"E2.13.0.0"),sQuery(id+"F0.wireOp",EDGE,"E2.13.0.1"),sQuery(id+"F0.wireOp",EDGE,"E2.13.0.2"),sQuery(id+"F0.wireOp",EDGE,"E2.13.0.3"),sQuery(id+"F0.wireOp",EDGE,"E2.14.0.0"),sQuery(id+"F0.wireOp",EDGE,"E2.14.0.1"),sQuery(id+"F0.wireOp",EDGE,"E2.14.0.2"),sQuery(id+"F0.wireOp",EDGE,"E2.14.0.3"),sQuery(id+"F0.wireOp",EDGE,"E2.15.0.0"),sQuery(id+"F0.wireOp",EDGE,"E2.15.0.1"),sQuery(id+"F0.wireOp",EDGE,"E2.15.0.2"),sQuery(id+"F0.wireOp",EDGE,"E2.15.0.3"),sQuery(id+"F0.wireOp",EDGE,"E2.16.0.0"),sQuery(id+"F0.wireOp",EDGE,"E2.16.0.1"),sQuery(id+"F0.wireOp",EDGE,"E2.16.0.2"),sQuery(id+"F0.wireOp",EDGE,"E2.16.0.3"),sQuery(id+"F0.wireOp",EDGE,"E2.17.0.0"),sQuery(id+"F0.wireOp",EDGE,"E2.17.0.1"),sQuery(id+"F0.wireOp",EDGE,"E2.17.0.2"),sQuery(id+"F0.wireOp",EDGE,"E2.17.0.3"),sQuery(id+"F0.wireOp",EDGE,"E2.18.0.0"),sQuery(id+"F0.wireOp",EDGE,"E2.18.0.1"),sQuery(id+"F0.wireOp",EDGE,"E2.18.0.2"),sQuery(id+"F0.wireOp",EDGE,"E2.18.0.3"),sQuery(id+"F0.wireOp",EDGE,"E2.19.0.0"),sQuery(id+"F0.wireOp",EDGE,"E2.19.0.1"),sQuery(id+"F0.wireOp",EDGE,"E2.19.0.2"),sQuery(id+"F0.wireOp",EDGE,"E2.19.0.3"),sQuery(id+"F0.wireOp",EDGE,"E2.20.0.0"),sQuery(id+"F0.wireOp",EDGE,"E2.20.0.1"),sQuery(id+"F0.wireOp",EDGE,"E2.20.0.2"),sQuery(id+"F0.wireOp",EDGE,"E2.20.0.3"),sQuery(id+"F0.wireOp",EDGE,"E2.21.0.0"),sQuery(id+"F0.wireOp",EDGE,"E2.21.0.1"),sQuery(id+"F0.wireOp",EDGE,"E2.21.0.2"),sQuery(id+"F0.wireOp",EDGE,"E2.21.0.3"),sQuery(id+"F0.wireOp",EDGE,"E2.22.0.0"),sQuery(id+"F0.wireOp",EDGE,"E2.22.0.1"),sQuery(id+"F0.wireOp",EDGE,"E2.22.0.2"),sQuery(id+"F0.wireOp",EDGE,"E2.22.0.3"),sQuery(id+"F0.wireOp",EDGE,"E2.23.0.0"),sQuery(id+"F0.wireOp",EDGE,"E2.23.0.1"),sQuery(id+"F0.wireOp",EDGE,"E2.23.0.2"),sQuery(id+"F0.wireOp",EDGE,"E2.23.0.3"),sQuery(id+"F0.wireOp",EDGE,"E2.24.0.0"),sQuery(id+"F0.wireOp",EDGE,"E2.24.0.1"),sQuery(id+"F0.wireOp",EDGE,"E2.24.0.2"),sQuery(id+"F0.wireOp",EDGE,"E2.24.0.3"),sQuery(id+"F0.wireOp",EDGE,"E2.25.0.0"),sQuery(id+"F0.wireOp",EDGE,"E2.25.0.1"),sQuery(id+"F0.wireOp",EDGE,"E2.25.0.2"),sQuery(id+"F0.wireOp",EDGE,"E2.25.0.3"),sQuery(id+"F0.wireOp",EDGE,"E2.26.0.0"),sQuery(id+"F0.wireOp",EDGE,"E2.26.0.1"),sQuery(id+"F0.wireOp",EDGE,"E2.26.0.2"),sQuery(id+"F0.wireOp",EDGE,"E2.26.0.3"),sQuery(id+"F0.wireOp",EDGE,"E2.27.0.0"),sQuery(id+"F0.wireOp",EDGE,"E2.27.0.1"),sQuery(id+"F0.wireOp",EDGE,"E2.27.0.2"),sQuery(id+"F0.wireOp",EDGE,"E2.27.0.3"),sQuery(id+"F0.wireOp",EDGE,"E2.28.0.0"),sQuery(id+"F0.wireOp",EDGE,"E2.28.0.1"),sQuery(id+"F0.wireOp",EDGE,"E2.28.0.2"),sQuery(id+"F0.wireOp",EDGE,"E2.28.0.3"),sQuery(id+"F0.wireOp",EDGE,"E2.29.0.0"),sQuery(id+"F0.wireOp",EDGE,"E2.29.0.1"),sQuery(id+"F0.wireOp",EDGE,"E2.29.0.2"),sQuery(id+"F0.wireOp",EDGE,"E2.29.0.3"),sQuery(id+"F0.wireOp",EDGE,"E2.30.0.0"),sQuery(id+"F0.wireOp",EDGE,"E2.30.0.1"),sQuery(id+"F0.wireOp",EDGE,"E2.30.0.2"),sQuery(id+"F0.wireOp",EDGE,"E2.30.0.3"),sQuery(id+"F0.wireOp",EDGE,"E2.31.0.0"),sQuery(id+"F0.wireOp",EDGE,"E2.31.0.1"),sQuery(id+"F0.wireOp",EDGE,"E2.31.0.2"),sQuery(id+"F0.wireOp",EDGE,"E2.31.0.3"),sQuery(id+"F0.wireOp",EDGE,"E2.32.0.0"),sQuery(id+"F0.wireOp",EDGE,"E2.32.0.1"),sQuery(id+"F0.wireOp",EDGE,"E2.32.0.2"),sQuery(id+"F0.wireOp",EDGE,"E2.32.0.3"),sQuery(id+"F0.wireOp",EDGE,"E2.33.0.0"),sQuery(id+"F0.wireOp",EDGE,"E2.33.0.1"),sQuery(id+"F0.wireOp",EDGE,"E2.33.0.2"),sQuery(id+"F0.wireOp",EDGE,"E2.33.0.3"),sQuery(id+"F0.wireOp",EDGE,"E2.34.0.0"),sQuery(id+"F0.wireOp",EDGE,"E2.34.0.1"),sQuery(id+"F0.wireOp",EDGE,"E2.34.0.2"),sQuery(id+"F0.wireOp",EDGE,"E2.34.0.3"),sQuery(id+"F0.wireOp",EDGE,"E2.35.0.0"),sQuery(id+"F0.wireOp",EDGE,"E2.35.0.1"),sQuery(id+"F0.wireOp",EDGE,"E2.35.0.2"),sQuery(id+"F0.wireOp",EDGE,"E2.35.0.3")])],"isStart":true});
            fillet(context, id + "F3", {"entities" : qUnion([Q0]), "radius" : 1 * mm, "tangentPropagation" : true, "allowEdgeOverflow" : false});
        }
        {
            var Q0;
            Q0=makeQuery(id+"F1.opExtrude","SWEPT_FACE",FACE,{"disambiguationData":[OSD([sQuery(id+"F0.wireOp",EDGE,"E0.right")])]});
            var sketch = newSketch(context, id + "F4", { "sketchPlane" : qUnion([Q0])});
            skPoint(sketch, "E3", {"position": v(-4, 12.5) * mm});
            skLineSegment(sketch, "E4.0.0", {"start": v(-10, 24) * mm, "end": v(-10, 1) * mm});
            skLineSegment(sketch, "E4.0.1", {"start": v(-10, 1) * mm, "end": v(10, 1) * mm});
            skLineSegment(sketch, "E4.0.2", {"start": v(10, 1) * mm, "end": v(10, 24) * mm});
            skLineSegment(sketch, "E4.0.3", {"start": v(10, 24) * mm, "end": v(-10, 24) * mm});
            skSolve(sketch);
        }
        {
            var Q0;
            Q0=sQuery(id+"F4.wireOp",VERTEX,"E3");
            var Q1;
            Q1=makeQuery(id+"F1.opExtrude","SWEPT_BODY",BODY,{"disambiguationData":[OSD([sQuery(id+"F0.wireOp",EDGE,"E0.bottom"),sQuery(id+"F0.wireOp",EDGE,"E0.top"),sQuery(id+"F0.wireOp",EDGE,"E0.left"),sQuery(id+"F0.wireOp",EDGE,"E0.right"),sQuery(id+"F0.wireOp",EDGE,"E1.bottom"),sQuery(id+"F0.wireOp",EDGE,"E1.top"),sQuery(id+"F0.wireOp",EDGE,"E1.left"),sQuery(id+"F0.wireOp",EDGE,"E1.right"),sQuery(id+"F0.wireOp",EDGE,"E2.1.0.0"),sQuery(id+"F0.wireOp",EDGE,"E2.1.0.1"),sQuery(id+"F0.wireOp",EDGE,"E2.1.0.2"),sQuery(id+"F0.wireOp",EDGE,"E2.1.0.3"),sQuery(id+"F0.wireOp",EDGE,"E2.2.0.0"),sQuery(id+"F0.wireOp",EDGE,"E2.2.0.1"),sQuery(id+"F0.wireOp",EDGE,"E2.2.0.2"),sQuery(id+"F0.wireOp",EDGE,"E2.2.0.3"),sQuery(id+"F0.wireOp",EDGE,"E2.3.0.0"),sQuery(id+"F0.wireOp",EDGE,"E2.3.0.1"),sQuery(id+"F0.wireOp",EDGE,"E2.3.0.2"),sQuery(id+"F0.wireOp",EDGE,"E2.3.0.3"),sQuery(id+"F0.wireOp",EDGE,"E2.4.0.0"),sQuery(id+"F0.wireOp",EDGE,"E2.4.0.1"),sQuery(id+"F0.wireOp",EDGE,"E2.4.0.2"),sQuery(id+"F0.wireOp",EDGE,"E2.4.0.3"),sQuery(id+"F0.wireOp",EDGE,"E2.5.0.0"),sQuery(id+"F0.wireOp",EDGE,"E2.5.0.1"),sQuery(id+"F0.wireOp",EDGE,"E2.5.0.2"),sQuery(id+"F0.wireOp",EDGE,"E2.5.0.3"),sQuery(id+"F0.wireOp",EDGE,"E2.6.0.0"),sQuery(id+"F0.wireOp",EDGE,"E2.6.0.1"),sQuery(id+"F0.wireOp",EDGE,"E2.6.0.2"),sQuery(id+"F0.wireOp",EDGE,"E2.6.0.3"),sQuery(id+"F0.wireOp",EDGE,"E2.7.0.0"),sQuery(id+"F0.wireOp",EDGE,"E2.7.0.1"),sQuery(id+"F0.wireOp",EDGE,"E2.7.0.2"),sQuery(id+"F0.wireOp",EDGE,"E2.7.0.3"),sQuery(id+"F0.wireOp",EDGE,"E2.8.0.0"),sQuery(id+"F0.wireOp",EDGE,"E2.8.0.1"),sQuery(id+"F0.wireOp",EDGE,"E2.8.0.2"),sQuery(id+"F0.wireOp",EDGE,"E2.8.0.3"),sQuery(id+"F0.wireOp",EDGE,"E2.9.0.0"),sQuery(id+"F0.wireOp",EDGE,"E2.9.0.1"),sQuery(id+"F0.wireOp",EDGE,"E2.9.0.2"),sQuery(id+"F0.wireOp",EDGE,"E2.9.0.3"),sQuery(id+"F0.wireOp",EDGE,"E2.10.0.0"),sQuery(id+"F0.wireOp",EDGE,"E2.10.0.1"),sQuery(id+"F0.wireOp",EDGE,"E2.10.0.2"),sQuery(id+"F0.wireOp",EDGE,"E2.10.0.3"),sQuery(id+"F0.wireOp",EDGE,"E2.11.0.0"),sQuery(id+"F0.wireOp",EDGE,"E2.11.0.1"),sQuery(id+"F0.wireOp",EDGE,"E2.11.0.2"),sQuery(id+"F0.wireOp",EDGE,"E2.11.0.3"),sQuery(id+"F0.wireOp",EDGE,"E2.12.0.0"),sQuery(id+"F0.wireOp",EDGE,"E2.12.0.1"),sQuery(id+"F0.wireOp",EDGE,"E2.12.0.2"),sQuery(id+"F0.wireOp",EDGE,"E2.12.0.3"),sQuery(id+"F0.wireOp",EDGE,"E2.13.0.0"),sQuery(id+"F0.wireOp",EDGE,"E2.13.0.1"),sQuery(id+"F0.wireOp",EDGE,"E2.13.0.2"),sQuery(id+"F0.wireOp",EDGE,"E2.13.0.3"),sQuery(id+"F0.wireOp",EDGE,"E2.14.0.0"),sQuery(id+"F0.wireOp",EDGE,"E2.14.0.1"),sQuery(id+"F0.wireOp",EDGE,"E2.14.0.2"),sQuery(id+"F0.wireOp",EDGE,"E2.14.0.3"),sQuery(id+"F0.wireOp",EDGE,"E2.15.0.0"),sQuery(id+"F0.wireOp",EDGE,"E2.15.0.1"),sQuery(id+"F0.wireOp",EDGE,"E2.15.0.2"),sQuery(id+"F0.wireOp",EDGE,"E2.15.0.3"),sQuery(id+"F0.wireOp",EDGE,"E2.16.0.0"),sQuery(id+"F0.wireOp",EDGE,"E2.16.0.1"),sQuery(id+"F0.wireOp",EDGE,"E2.16.0.2"),sQuery(id+"F0.wireOp",EDGE,"E2.16.0.3"),sQuery(id+"F0.wireOp",EDGE,"E2.17.0.0"),sQuery(id+"F0.wireOp",EDGE,"E2.17.0.1"),sQuery(id+"F0.wireOp",EDGE,"E2.17.0.2"),sQuery(id+"F0.wireOp",EDGE,"E2.17.0.3"),sQuery(id+"F0.wireOp",EDGE,"E2.18.0.0"),sQuery(id+"F0.wireOp",EDGE,"E2.18.0.1"),sQuery(id+"F0.wireOp",EDGE,"E2.18.0.2"),sQuery(id+"F0.wireOp",EDGE,"E2.18.0.3"),sQuery(id+"F0.wireOp",EDGE,"E2.19.0.0"),sQuery(id+"F0.wireOp",EDGE,"E2.19.0.1"),sQuery(id+"F0.wireOp",EDGE,"E2.19.0.2"),sQuery(id+"F0.wireOp",EDGE,"E2.19.0.3"),sQuery(id+"F0.wireOp",EDGE,"E2.20.0.0"),sQuery(id+"F0.wireOp",EDGE,"E2.20.0.1"),sQuery(id+"F0.wireOp",EDGE,"E2.20.0.2"),sQuery(id+"F0.wireOp",EDGE,"E2.20.0.3"),sQuery(id+"F0.wireOp",EDGE,"E2.21.0.0"),sQuery(id+"F0.wireOp",EDGE,"E2.21.0.1"),sQuery(id+"F0.wireOp",EDGE,"E2.21.0.2"),sQuery(id+"F0.wireOp",EDGE,"E2.21.0.3"),sQuery(id+"F0.wireOp",EDGE,"E2.22.0.0"),sQuery(id+"F0.wireOp",EDGE,"E2.22.0.1"),sQuery(id+"F0.wireOp",EDGE,"E2.22.0.2"),sQuery(id+"F0.wireOp",EDGE,"E2.22.0.3"),sQuery(id+"F0.wireOp",EDGE,"E2.23.0.0"),sQuery(id+"F0.wireOp",EDGE,"E2.23.0.1"),sQuery(id+"F0.wireOp",EDGE,"E2.23.0.2"),sQuery(id+"F0.wireOp",EDGE,"E2.23.0.3"),sQuery(id+"F0.wireOp",EDGE,"E2.24.0.0"),sQuery(id+"F0.wireOp",EDGE,"E2.24.0.1"),sQuery(id+"F0.wireOp",EDGE,"E2.24.0.2"),sQuery(id+"F0.wireOp",EDGE,"E2.24.0.3"),sQuery(id+"F0.wireOp",EDGE,"E2.25.0.0"),sQuery(id+"F0.wireOp",EDGE,"E2.25.0.1"),sQuery(id+"F0.wireOp",EDGE,"E2.25.0.2"),sQuery(id+"F0.wireOp",EDGE,"E2.25.0.3"),sQuery(id+"F0.wireOp",EDGE,"E2.26.0.0"),sQuery(id+"F0.wireOp",EDGE,"E2.26.0.1"),sQuery(id+"F0.wireOp",EDGE,"E2.26.0.2"),sQuery(id+"F0.wireOp",EDGE,"E2.26.0.3"),sQuery(id+"F0.wireOp",EDGE,"E2.27.0.0"),sQuery(id+"F0.wireOp",EDGE,"E2.27.0.1"),sQuery(id+"F0.wireOp",EDGE,"E2.27.0.2"),sQuery(id+"F0.wireOp",EDGE,"E2.27.0.3"),sQuery(id+"F0.wireOp",EDGE,"E2.28.0.0"),sQuery(id+"F0.wireOp",EDGE,"E2.28.0.1"),sQuery(id+"F0.wireOp",EDGE,"E2.28.0.2"),sQuery(id+"F0.wireOp",EDGE,"E2.28.0.3"),sQuery(id+"F0.wireOp",EDGE,"E2.29.0.0"),sQuery(id+"F0.wireOp",EDGE,"E2.29.0.1"),sQuery(id+"F0.wireOp",EDGE,"E2.29.0.2"),sQuery(id+"F0.wireOp",EDGE,"E2.29.0.3"),sQuery(id+"F0.wireOp",EDGE,"E2.30.0.0"),sQuery(id+"F0.wireOp",EDGE,"E2.30.0.1"),sQuery(id+"F0.wireOp",EDGE,"E2.30.0.2"),sQuery(id+"F0.wireOp",EDGE,"E2.30.0.3"),sQuery(id+"F0.wireOp",EDGE,"E2.31.0.0"),sQuery(id+"F0.wireOp",EDGE,"E2.31.0.1"),sQuery(id+"F0.wireOp",EDGE,"E2.31.0.2"),sQuery(id+"F0.wireOp",EDGE,"E2.31.0.3"),sQuery(id+"F0.wireOp",EDGE,"E2.32.0.0"),sQuery(id+"F0.wireOp",EDGE,"E2.32.0.1"),sQuery(id+"F0.wireOp",EDGE,"E2.32.0.2"),sQuery(id+"F0.wireOp",EDGE,"E2.32.0.3"),sQuery(id+"F0.wireOp",EDGE,"E2.33.0.0"),sQuery(id+"F0.wireOp",EDGE,"E2.33.0.1"),sQuery(id+"F0.wireOp",EDGE,"E2.33.0.2"),sQuery(id+"F0.wireOp",EDGE,"E2.33.0.3"),sQuery(id+"F0.wireOp",EDGE,"E2.34.0.0"),sQuery(id+"F0.wireOp",EDGE,"E2.34.0.1"),sQuery(id+"F0.wireOp",EDGE,"E2.34.0.2"),sQuery(id+"F0.wireOp",EDGE,"E2.34.0.3"),sQuery(id+"F0.wireOp",EDGE,"E2.35.0.0"),sQuery(id+"F0.wireOp",EDGE,"E2.35.0.1"),sQuery(id+"F0.wireOp",EDGE,"E2.35.0.2"),sQuery(id+"F0.wireOp",EDGE,"E2.35.0.3")])]});
            hole(context, id + "F5", {"style" : HoleStyle.SIMPLE, "endStyle" : HoleEndStyle.THROUGH, "holeDiameter" : 5 * mm, "majorDiameter" : 5 * mm, "isTappedThrough" : true, "tappedDepth" : 26.25 * mm, "tapClearance" : 3, "locations" : qUnion([Q0]), "scope" : qUnion([Q1]), "startStyle" : HoleStartStyle.PART});
        }
    });
